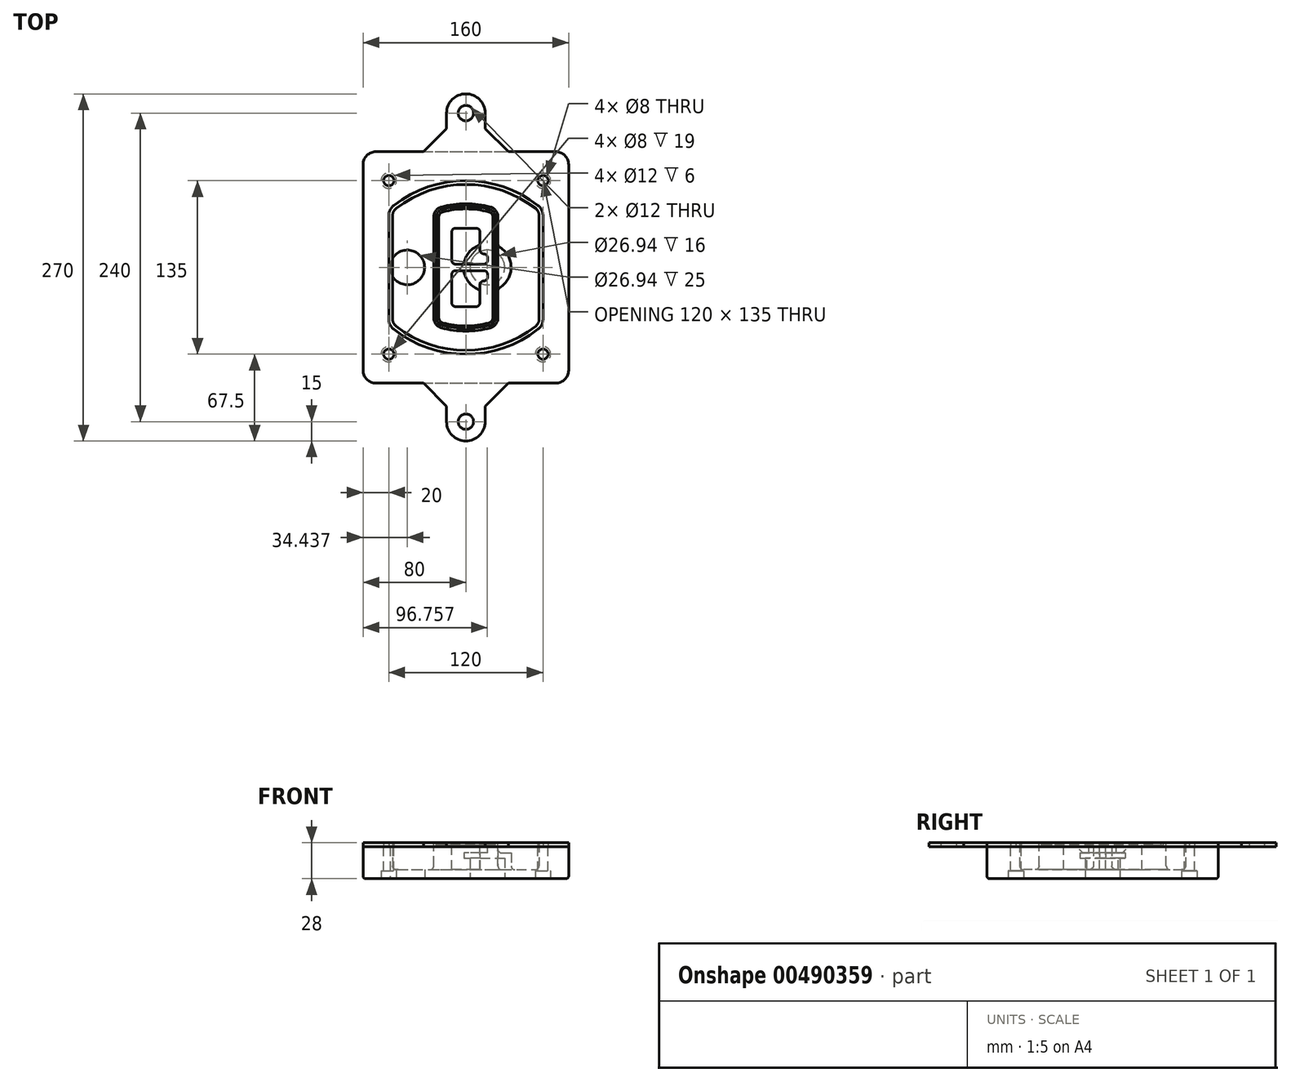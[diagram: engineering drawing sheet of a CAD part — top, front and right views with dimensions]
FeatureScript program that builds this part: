
annotation { "Feature Type Name" : "Feature", "Feature Type Description" : "" }
export const myFeature = defineFeature(function(context is Context, id is Id, definition is map)
    precondition{}
    {
        {
            var Q0;
            Q0=qCreatedBy(makeId("Top.planeOp"),FACE);
            var sketch = newSketch(context, id + "F0", { "sketchPlane" : qUnion([Q0])});
            skPoint(sketch, "E0.rect.middle", {"position": v(0, 0) * mm});
            skLineSegment(sketch, "E1.bottom", {"start": v(-70, -90) * mm, "end": v(70, -90) * mm});
            skLineSegment(sketch, "E1.top", {"start": v(-70, 90) * mm, "end": v(70, 90) * mm});
            skLineSegment(sketch, "E1.left", {"start": v(-80, -80) * mm, "end": v(-80, 80) * mm});
            skLineSegment(sketch, "E1.right", {"start": v(80, -80) * mm, "end": v(80, 80) * mm});
            skLineSegment(sketch, "E2", {"start": v(-80, 90) * mm, "end": v(80, -90) * mm, "construction": true});
            skLineSegment(sketch, "E3", {"start": v(80, 90) * mm, "end": v(-80, -90) * mm, "construction": true});
            skCircle(sketch, "E4", {"center": v(-60, 67.5) * mm, "radius": 4 * mm});
            skCircle(sketch, "E5", {"center": v(60, 67.5) * mm, "radius": 4 * mm});
            skCircle(sketch, "E6", {"center": v(60, -67.5) * mm, "radius": 4 * mm});
            skCircle(sketch, "E7", {"center": v(-60, -67.5) * mm, "radius": 4 * mm});
            skLineSegment(sketch, "E8", {"start": v(-60, 67.5) * mm, "end": v(60, 67.5) * mm, "construction": true});
            skLineSegment(sketch, "E9", {"start": v(60, 67.5) * mm, "end": v(60, -67.5) * mm, "construction": true});
            skLineSegment(sketch, "E10", {"start": v(60, -67.5) * mm, "end": v(-60, -67.5) * mm, "construction": true});
            skLineSegment(sketch, "E11", {"start": v(-60, -67.5) * mm, "end": v(-60, 67.5) * mm, "construction": true});
            skLineSegment(sketch, "E12", {"start": v(-60, 40.3) * mm, "end": v(-60, -40.3) * mm});
            skLineSegment(sketch, "E13", {"start": v(60, 40.3) * mm, "end": v(60, -40.3) * mm});
            skArc(sketch, "E14", {"start": v(56.15, 48.18) * mm, "mid": v(0, 67.5) * mm, "end": v(-56.15, 48.18) * mm});
            skArc(sketch, "E15", {"start": v(-56.15, -48.18) * mm, "mid": v(0, -67.5) * mm, "end": v(56.15, -48.18) * mm});
            skLineSegment(sketch, "E16", {"start": v(-60, 0) * mm, "end": v(60, 0) * mm, "construction": true});
            skPoint(sketch, "E17.visualSharp", {"position": v(-60, -45) * mm});
            skArc(sketch, "E17.filletArc", {"start": v(-60, -40.3) * mm, "mid": v(-58.99, -44.68) * mm, "end": v(-56.15, -48.18) * mm});
            skPoint(sketch, "E18.visualSharp", {"position": v(-60, 45) * mm});
            skArc(sketch, "E18.filletArc", {"start": v(-56.15, 48.18) * mm, "mid": v(-58.99, 44.68) * mm, "end": v(-60, 40.3) * mm});
            skPoint(sketch, "E19.visualSharp", {"position": v(60, 45) * mm});
            skArc(sketch, "E19.filletArc", {"start": v(60, 40.3) * mm, "mid": v(58.99, 44.68) * mm, "end": v(56.15, 48.18) * mm});
            skPoint(sketch, "E20.visualSharp", {"position": v(60, -45) * mm});
            skArc(sketch, "E20.filletArc", {"start": v(56.15, -48.18) * mm, "mid": v(58.99, -44.68) * mm, "end": v(60, -40.3) * mm});
            skPoint(sketch, "E21.visualSharp", {"position": v(-80, 90) * mm});
            skArc(sketch, "E21.filletArc", {"start": v(-70, 90) * mm, "mid": v(-77.07, 87.07) * mm, "end": v(-80, 80) * mm});
            skPoint(sketch, "E22.visualSharp", {"position": v(80, 90) * mm});
            skArc(sketch, "E22.filletArc", {"start": v(80, 80) * mm, "mid": v(77.07, 87.07) * mm, "end": v(70, 90) * mm});
            skPoint(sketch, "E23.visualSharp", {"position": v(80, -90) * mm});
            skArc(sketch, "E23.filletArc", {"start": v(70, -90) * mm, "mid": v(77.07, -87.07) * mm, "end": v(80, -80) * mm});
            skPoint(sketch, "E24.visualSharp", {"position": v(-80, -90) * mm});
            skArc(sketch, "E24.filletArc", {"start": v(-80, -80) * mm, "mid": v(-77.07, -87.07) * mm, "end": v(-70, -90) * mm});
            skArc(sketch, "E25.0", {"start": v(57, 40.3) * mm, "mid": v(56.3, 43.36) * mm, "end": v(54.3, 45.81) * mm});
            skLineSegment(sketch, "E25.1", {"start": v(57, 40.3) * mm, "end": v(57, -40.3) * mm});
            skArc(sketch, "E25.2", {"start": v(54.3, -45.81) * mm, "mid": v(56.3, -43.36) * mm, "end": v(57, -40.3) * mm});
            skArc(sketch, "E25.3", {"start": v(-54.3, -45.81) * mm, "mid": v(0, -64.5) * mm, "end": v(54.3, -45.81) * mm});
            skArc(sketch, "E25.4", {"start": v(-57, -40.3) * mm, "mid": v(-56.3, -43.36) * mm, "end": v(-54.3, -45.81) * mm});
            skArc(sketch, "E25.5", {"start": v(54.3, 45.81) * mm, "mid": v(0, 64.5) * mm, "end": v(-54.3, 45.81) * mm});
            skLineSegment(sketch, "E25.6", {"start": v(-57, 40.3) * mm, "end": v(-57, -40.3) * mm});
            skArc(sketch, "E25.7", {"start": v(-54.3, 45.81) * mm, "mid": v(-56.3, 43.36) * mm, "end": v(-57, 40.3) * mm});
            skArc(sketch, "E26.0", {"start": v(-58.62, 51.33) * mm, "mid": v(-62.58, 46.43) * mm, "end": v(-64, 40.3) * mm});
            skArc(sketch, "E26.1", {"start": v(58.62, 51.33) * mm, "mid": v(0, 71.5) * mm, "end": v(-58.62, 51.33) * mm});
            skArc(sketch, "E26.2", {"start": v(64, 40.3) * mm, "mid": v(62.58, 46.43) * mm, "end": v(58.62, 51.33) * mm});
            skLineSegment(sketch, "E26.3", {"start": v(64, 40.3) * mm, "end": v(64, -40.3) * mm});
            skArc(sketch, "E26.4", {"start": v(58.62, -51.33) * mm, "mid": v(62.58, -46.43) * mm, "end": v(64, -40.3) * mm});
            skLineSegment(sketch, "E26.5", {"start": v(-64, 40.3) * mm, "end": v(-64, -40.3) * mm});
            skArc(sketch, "E26.6", {"start": v(-58.62, -51.33) * mm, "mid": v(0, -71.5) * mm, "end": v(58.62, -51.33) * mm});
            skArc(sketch, "E26.7", {"start": v(-64, -40.3) * mm, "mid": v(-62.58, -46.43) * mm, "end": v(-58.62, -51.33) * mm});
            skSolve(sketch);
        }
        {
            var Q0;
            Q0=makeQuery(id+"F0.imprint","IMPRINT",FACE,{"disambiguationData":[TD([[makeQuery(id+"F0.imprint","IMPRINT",EDGE,{"derivedFrom":sQuery(id+"F0.wireOp",EDGE,"E1.bottom")}),1.0]])]});
            var Q1;
            Q1=makeQuery(id+"F0.imprint","IMPRINT",FACE,{"disambiguationData":[TD([[makeQuery(id+"F0.imprint","IMPRINT",EDGE,{"derivedFrom":sQuery(id+"F0.wireOp",EDGE,"E12")}),1.0]])]});
            var Q2;
            Q2=makeQuery(id+"F0.imprint","IMPRINT",FACE,{"disambiguationData":[TD([[makeQuery(id+"F0.imprint","IMPRINT",EDGE,{"derivedFrom":sQuery(id+"F0.wireOp",EDGE,"E25.0")}),1.0]])]});
            var Q3;
            Q3=makeQuery(id+"F0.imprint","IMPRINT",FACE,{"disambiguationData":[TD([[makeQuery(id+"F0.imprint","IMPRINT",EDGE,{"derivedFrom":sQuery(id+"F0.wireOp",EDGE,"E12")}),-1.0]])]});
            extrude(context, id + "F1", {"entities" : qUnion([Q0, Q1, Q2, Q3]), "oppositeDirection" : true, "depth" : 25 * mm});
        }
        {
            var Q0;
            Q0=makeQuery(id+"F0.imprint","IMPRINT",FACE,{"disambiguationData":[TD([[makeQuery(id+"F0.imprint","IMPRINT",EDGE,{"derivedFrom":sQuery(id+"F0.wireOp",EDGE,"E12")}),1.0]])]});
            extrude(context, id + "F2", {"entities" : qUnion([Q0]), "operationType" : NewBodyOperationType.ADD, "depth" : 3 * mm});
        }
        {
            var Q0;
            Q0=makeQuery(id+"F0.imprint","IMPRINT",FACE,{"disambiguationData":[TD([[makeQuery(id+"F0.imprint","IMPRINT",EDGE,{"derivedFrom":sQuery(id+"F0.wireOp",EDGE,"E25.0")}),1.0]])]});
            extrude(context, id + "F3", {"entities" : qUnion([Q0]), "operationType" : NewBodyOperationType.REMOVE, "oppositeDirection" : true, "depth" : 18 * mm});
        }
        {
            var Q0;
            Q0=makeQuery(id+"F2.opExtrude","CAP_FACE",FACE,{"disambiguationData":[OSD([sQuery(id+"F0.wireOp",EDGE,"E12"),sQuery(id+"F0.wireOp",EDGE,"E13"),sQuery(id+"F0.wireOp",EDGE,"E14"),sQuery(id+"F0.wireOp",EDGE,"E15"),sQuery(id+"F0.wireOp",EDGE,"E17.filletArc"),sQuery(id+"F0.wireOp",EDGE,"E18.filletArc"),sQuery(id+"F0.wireOp",EDGE,"E19.filletArc"),sQuery(id+"F0.wireOp",EDGE,"E20.filletArc"),sQuery(id+"F0.wireOp",EDGE,"E25.0"),sQuery(id+"F0.wireOp",EDGE,"E25.1"),sQuery(id+"F0.wireOp",EDGE,"E25.2"),sQuery(id+"F0.wireOp",EDGE,"E25.3"),sQuery(id+"F0.wireOp",EDGE,"E25.4"),sQuery(id+"F0.wireOp",EDGE,"E25.5"),sQuery(id+"F0.wireOp",EDGE,"E25.6"),sQuery(id+"F0.wireOp",EDGE,"E25.7")])],"isStart":false});
            var sketch = newSketch(context, id + "F4", { "sketchPlane" : qUnion([Q0])});
            skArc(sketch, "E27.0", {"start": v(-19.08, -46.97) * mm, "mid": v(0, -49.5) * mm, "end": v(19.08, -46.97) * mm});
            skArc(sketch, "E28.0", {"start": v(19.08, 46.97) * mm, "mid": v(0, 49.5) * mm, "end": v(-19.08, 46.97) * mm});
            skLineSegment(sketch, "E29", {"start": v(-25, 39.25) * mm, "end": v(-25, -39.25) * mm});
            skLineSegment(sketch, "E30", {"start": v(25, 39.25) * mm, "end": v(25, -39.25) * mm});
            skLineSegment(sketch, "E31", {"start": v(-25, 45.1) * mm, "end": v(25, 45.1) * mm, "construction": true});
            skLineSegment(sketch, "E32", {"start": v(-25, -45.1) * mm, "end": v(25, -45.1) * mm, "construction": true});
            skPoint(sketch, "E33.visualSharp", {"position": v(-25, 45.1) * mm});
            skArc(sketch, "E33.filletArc", {"start": v(-19.08, 46.97) * mm, "mid": v(-23.35, 44.11) * mm, "end": v(-25, 39.25) * mm});
            skPoint(sketch, "E34.visualSharp", {"position": v(25, 45.1) * mm});
            skArc(sketch, "E34.filletArc", {"start": v(25, 39.25) * mm, "mid": v(23.35, 44.11) * mm, "end": v(19.08, 46.97) * mm});
            skPoint(sketch, "E35.visualSharp", {"position": v(25, -45.1) * mm});
            skArc(sketch, "E35.filletArc", {"start": v(19.08, -46.97) * mm, "mid": v(23.35, -44.11) * mm, "end": v(25, -39.25) * mm});
            skPoint(sketch, "E36.visualSharp", {"position": v(-25, -45.1) * mm});
            skArc(sketch, "E36.filletArc", {"start": v(-25, -39.25) * mm, "mid": v(-23.35, -44.11) * mm, "end": v(-19.08, -46.97) * mm});
            skArc(sketch, "E37.0", {"start": v(54.3, 45.81) * mm, "mid": v(0, 64.5) * mm, "end": v(-54.3, 45.81) * mm});
            skArc(sketch, "E37.1", {"start": v(-54.3, 45.81) * mm, "mid": v(-56.3, 43.36) * mm, "end": v(-57, 40.3) * mm});
            skLineSegment(sketch, "E37.2", {"start": v(-57, 40.3) * mm, "end": v(-57, -40.3) * mm});
            skArc(sketch, "E37.3", {"start": v(-57, -40.3) * mm, "mid": v(-56.3, -43.36) * mm, "end": v(-54.3, -45.81) * mm});
            skArc(sketch, "E37.4", {"start": v(-54.3, -45.81) * mm, "mid": v(0, -64.5) * mm, "end": v(54.3, -45.81) * mm});
            skArc(sketch, "E37.5", {"start": v(54.3, -45.81) * mm, "mid": v(56.3, -43.36) * mm, "end": v(57, -40.3) * mm});
            skLineSegment(sketch, "E37.6", {"start": v(57, 40.3) * mm, "end": v(57, -40.3) * mm});
            skArc(sketch, "E37.7", {"start": v(57, 40.3) * mm, "mid": v(56.3, 43.36) * mm, "end": v(54.3, 45.81) * mm});
            skLineSegment(sketch, "E38.0", {"start": v(23, 39.25) * mm, "end": v(23, -39.25) * mm});
            skArc(sketch, "E38.1", {"start": v(18.56, -45.04) * mm, "mid": v(21.76, -42.9) * mm, "end": v(23, -39.25) * mm});
            skArc(sketch, "E38.2", {"start": v(-18.56, -45.04) * mm, "mid": v(0, -47.5) * mm, "end": v(18.56, -45.04) * mm});
            skArc(sketch, "E38.3", {"start": v(-23, -39.25) * mm, "mid": v(-21.76, -42.9) * mm, "end": v(-18.56, -45.04) * mm});
            skLineSegment(sketch, "E38.4", {"start": v(-23, 39.25) * mm, "end": v(-23, -39.25) * mm});
            skArc(sketch, "E38.5", {"start": v(23, 39.25) * mm, "mid": v(21.76, 42.9) * mm, "end": v(18.56, 45.04) * mm});
            skArc(sketch, "E38.6", {"start": v(-18.56, 45.04) * mm, "mid": v(-21.76, 42.9) * mm, "end": v(-23, 39.25) * mm});
            skArc(sketch, "E38.7", {"start": v(18.56, 45.04) * mm, "mid": v(0, 47.5) * mm, "end": v(-18.56, 45.04) * mm});
            skArc(sketch, "E39.0", {"start": v(21, 39.25) * mm, "mid": v(20.18, 41.68) * mm, "end": v(18.04, 43.1) * mm});
            skLineSegment(sketch, "E39.1", {"start": v(21, 39.25) * mm, "end": v(21, -39.25) * mm});
            skArc(sketch, "E39.2", {"start": v(18.04, -43.1) * mm, "mid": v(20.18, -41.68) * mm, "end": v(21, -39.25) * mm});
            skArc(sketch, "E39.3", {"start": v(-18.04, -43.1) * mm, "mid": v(0, -45.5) * mm, "end": v(18.04, -43.1) * mm});
            skArc(sketch, "E39.4", {"start": v(-21, -39.25) * mm, "mid": v(-20.18, -41.68) * mm, "end": v(-18.04, -43.1) * mm});
            skArc(sketch, "E39.5", {"start": v(18.04, 43.1) * mm, "mid": v(0, 45.5) * mm, "end": v(-18.04, 43.1) * mm});
            skLineSegment(sketch, "E39.6", {"start": v(-21, 39.25) * mm, "end": v(-21, -39.25) * mm});
            skArc(sketch, "E39.7", {"start": v(-18.04, 43.1) * mm, "mid": v(-20.18, 41.68) * mm, "end": v(-21, 39.25) * mm});
            skLineSegment(sketch, "E40", {"start": v(-25, 0) * mm, "end": v(25, 0) * mm, "construction": true});
            skLineSegment(sketch, "E41", {"start": v(-11, 5.5) * mm, "end": v(-11, 27.5) * mm});
            skLineSegment(sketch, "E42", {"start": v(-8, 30.5) * mm, "end": v(8, 30.5) * mm});
            skLineSegment(sketch, "E43", {"start": v(11, 27.5) * mm, "end": v(11, 13.5) * mm});
            skLineSegment(sketch, "E44", {"start": v(14, 10.5) * mm, "end": v(14, 10.5) * mm});
            skLineSegment(sketch, "E45", {"start": v(17, 7.5) * mm, "end": v(17, 5.5) * mm});
            skLineSegment(sketch, "E46", {"start": v(14, 2.5) * mm, "end": v(-8, 2.5) * mm});
            skPoint(sketch, "E47.visualSharp", {"position": v(-11, 30.5) * mm});
            skArc(sketch, "E47.filletArc", {"start": v(-8, 30.5) * mm, "mid": v(-10.12, 29.62) * mm, "end": v(-11, 27.5) * mm});
            skPoint(sketch, "E48.visualSharp", {"position": v(11, 30.5) * mm});
            skArc(sketch, "E48.filletArc", {"start": v(11, 27.5) * mm, "mid": v(10.12, 29.62) * mm, "end": v(8, 30.5) * mm});
            skPoint(sketch, "E49.visualSharp", {"position": v(11, 10.5) * mm});
            skArc(sketch, "E49.filletArc", {"start": v(11, 13.5) * mm, "mid": v(11.88, 11.38) * mm, "end": v(14, 10.5) * mm});
            skPoint(sketch, "E50.visualSharp", {"position": v(17, 10.5) * mm});
            skArc(sketch, "E50.filletArc", {"start": v(17, 7.5) * mm, "mid": v(16.12, 9.62) * mm, "end": v(14, 10.5) * mm});
            skPoint(sketch, "E51.visualSharp", {"position": v(17, 2.5) * mm});
            skArc(sketch, "E51.filletArc", {"start": v(14, 2.5) * mm, "mid": v(16.12, 3.38) * mm, "end": v(17, 5.5) * mm});
            skPoint(sketch, "E52.visualSharp", {"position": v(-11, 2.5) * mm});
            skArc(sketch, "E52.filletArc", {"start": v(-11, 5.5) * mm, "mid": v(-10.12, 3.38) * mm, "end": v(-8, 2.5) * mm});
            skLineSegment(sketch, "E53.0.MirrorCS", {"start": v(14, -2.5) * mm, "end": v(-8, -2.5) * mm});
            skArc(sketch, "E54.0.MirrorCS", {"start": v(-11, -5.5) * mm, "mid": v(-10.12, -3.38) * mm, "end": v(-8, -2.5) * mm});
            skLineSegment(sketch, "E55.0.MirrorCS", {"start": v(-11, -5.5) * mm, "end": v(-11, -27.5) * mm});
            skArc(sketch, "E56.0.MirrorCS", {"start": v(-8, -30.5) * mm, "mid": v(-10.12, -29.62) * mm, "end": v(-11, -27.5) * mm});
            skLineSegment(sketch, "E57.0.MirrorCS", {"start": v(-8, -30.5) * mm, "end": v(8, -30.5) * mm});
            skArc(sketch, "E58.0.MirrorCS", {"start": v(11, -27.5) * mm, "mid": v(10.12, -29.62) * mm, "end": v(8, -30.5) * mm});
            skLineSegment(sketch, "E59.0.MirrorCS", {"start": v(11, -27.5) * mm, "end": v(11, -13.5) * mm});
            skArc(sketch, "E60.0.MirrorCS", {"start": v(11, -13.5) * mm, "mid": v(11.88, -11.38) * mm, "end": v(14, -10.5) * mm});
            skArc(sketch, "E61.0.MirrorCS", {"start": v(17, -7.5) * mm, "mid": v(16.12, -9.62) * mm, "end": v(14, -10.5) * mm});
            skLineSegment(sketch, "E62.0.MirrorCS", {"start": v(17, -7.5) * mm, "end": v(17, -5.5) * mm});
            skArc(sketch, "E63.0.MirrorCS", {"start": v(14, -2.5) * mm, "mid": v(16.12, -3.38) * mm, "end": v(17, -5.5) * mm});
            skSolve(sketch);
        }
        {
            var Q0;
            Q0=makeQuery(id+"F4.imprint","IMPRINT",FACE,{"disambiguationData":[TD([[makeQuery(id+"F4.imprint","IMPRINT",EDGE,{"derivedFrom":sQuery(id+"F4.wireOp",EDGE,"E27.0")}),1.0]])]});
            var Q1;
            Q1=makeQuery(id+"F4.imprint","IMPRINT",FACE,{"disambiguationData":[TD([[makeQuery(id+"F4.imprint","IMPRINT",EDGE,{"derivedFrom":sQuery(id+"F4.wireOp",EDGE,"E38.0")}),-1.0]])]});
            var Q2;
            Q2=makeQuery(id+"F4.imprint","IMPRINT",FACE,{"disambiguationData":[TD([[makeQuery(id+"F4.imprint","IMPRINT",EDGE,{"derivedFrom":sQuery(id+"F4.wireOp",EDGE,"E39.0")}),1.0]])]});
            extrude(context, id + "F5", {"entities" : qUnion([Q0, Q1, Q2]), "operationType" : NewBodyOperationType.ADD, "endBound" : BoundingType.UP_TO_NEXT, "oppositeDirection" : true, "depth" : 25 * mm});
        }
        {
            var Q0;
            Q0=makeQuery(id+"F4.imprint","IMPRINT",FACE,{"disambiguationData":[TD([[makeQuery(id+"F4.imprint","IMPRINT",EDGE,{"derivedFrom":sQuery(id+"F4.wireOp",EDGE,"E38.0")}),-1.0]])]});
            extrude(context, id + "F6", {"entities" : qUnion([Q0]), "operationType" : NewBodyOperationType.REMOVE, "oppositeDirection" : true, "depth" : 2 * mm});
        }
        {
            var Q0;
            Q0=makeQuery(id+"F1.opExtrude","CAP_FACE",FACE,{"disambiguationData":[OSD([sQuery(id+"F0.wireOp",EDGE,"E1.bottom"),sQuery(id+"F0.wireOp",EDGE,"E1.top"),sQuery(id+"F0.wireOp",EDGE,"E1.left"),sQuery(id+"F0.wireOp",EDGE,"E1.right"),sQuery(id+"F0.wireOp",EDGE,"E4"),sQuery(id+"F0.wireOp",EDGE,"E5"),sQuery(id+"F0.wireOp",EDGE,"E6"),sQuery(id+"F0.wireOp",EDGE,"E7"),sQuery(id+"F0.wireOp",EDGE,"E21.filletArc"),sQuery(id+"F0.wireOp",EDGE,"E22.filletArc"),sQuery(id+"F0.wireOp",EDGE,"E23.filletArc"),sQuery(id+"F0.wireOp",EDGE,"E24.filletArc")])],"isStart":false});
            var sketch = newSketch(context, id + "F7", { "sketchPlane" : qUnion([Q0])});
            skCircle(sketch, "E64", {"center": v(16.76, 0) * mm, "radius": 13.47 * mm});
            skCircle(sketch, "E65", {"center": v(-45.56, 0) * mm, "radius": 13.47 * mm});
            skLineSegment(sketch, "E66", {"start": v(80, 0) * mm, "end": v(-80, 0) * mm});
            skCircle(sketch, "E67", {"center": v(16.76, 0) * mm, "radius": 18.47 * mm});
            skCircle(sketch, "E68", {"center": v(60, -67.5) * mm, "radius": 6 * mm});
            skCircle(sketch, "E69", {"center": v(-60, -67.5) * mm, "radius": 6 * mm});
            skCircle(sketch, "E70", {"center": v(-60, 67.5) * mm, "radius": 6 * mm});
            skCircle(sketch, "E71", {"center": v(60, 67.5) * mm, "radius": 6 * mm});
            skSolve(sketch);
        }
        {
            var Q0;
            {var subQ1=sQuery(id+"F7.wireOp",EDGE,"E66");var subQ4=sQuery(id+"F7.wireOp",EDGE,"E64");var subQ6=makeQuery(id+"F7.imprint","INTERSECT",VERTEX,{"disambiguationData":[OD(0.0)],"derivedFrom":[subQ4,subQ1]});Q0=makeQuery(id+"F7.imprint","IMPRINT",FACE,{"disambiguationData":[TD([[makeQuery(id+"F7.imprint","IMPRINT",EDGE,{"disambiguationData":[TD([[subQ6,-1.0]])],"derivedFrom":subQ4}),-1.0]])]});}
            var Q1;
            {var subQ0=sQuery(id+"F7.wireOp",EDGE,"E66");var subQ1=sQuery(id+"F7.wireOp",EDGE,"E64");var subQ3=makeQuery(id+"F7.imprint","INTERSECT",VERTEX,{"disambiguationData":[OD(0.0)],"derivedFrom":[subQ1,subQ0]});Q1=makeQuery(id+"F7.imprint","IMPRINT",FACE,{"disambiguationData":[TD([[makeQuery(id+"F7.imprint","IMPRINT",EDGE,{"disambiguationData":[TD([[subQ3,-1.0]])],"derivedFrom":subQ1}),1.0]])]});}
            var Q2;
            {var subQ0=sQuery(id+"F7.wireOp",EDGE,"E66");var subQ1=sQuery(id+"F7.wireOp",EDGE,"E64");var subQ3=makeQuery(id+"F7.imprint","INTERSECT",VERTEX,{"disambiguationData":[OD(0.0)],"derivedFrom":[subQ1,subQ0]});Q2=makeQuery(id+"F7.imprint","IMPRINT",FACE,{"disambiguationData":[TD([[makeQuery(id+"F7.imprint","IMPRINT",EDGE,{"disambiguationData":[TD([[subQ3,1.0]])],"derivedFrom":subQ1}),1.0]])]});}
            var Q3;
            {var subQ1=sQuery(id+"F7.wireOp",EDGE,"E66");var subQ4=sQuery(id+"F7.wireOp",EDGE,"E64");var subQ6=makeQuery(id+"F7.imprint","INTERSECT",VERTEX,{"disambiguationData":[OD(0.0)],"derivedFrom":[subQ4,subQ1]});Q3=makeQuery(id+"F7.imprint","IMPRINT",FACE,{"disambiguationData":[TD([[makeQuery(id+"F7.imprint","IMPRINT",EDGE,{"disambiguationData":[TD([[subQ6,1.0]])],"derivedFrom":subQ4}),-1.0]])]});}
            extrude(context, id + "F8", {"entities" : qUnion([Q0, Q1, Q2, Q3]), "operationType" : NewBodyOperationType.ADD, "oppositeDirection" : true, "depth" : 20 * mm});
        }
        {
            var Q0;
            {var subQ0=sQuery(id+"F7.wireOp",EDGE,"E66");var subQ1=sQuery(id+"F7.wireOp",EDGE,"E64");var subQ3=makeQuery(id+"F7.imprint","INTERSECT",VERTEX,{"disambiguationData":[OD(0.0)],"derivedFrom":[subQ1,subQ0]});Q0=makeQuery(id+"F7.imprint","IMPRINT",FACE,{"disambiguationData":[TD([[makeQuery(id+"F7.imprint","IMPRINT",EDGE,{"disambiguationData":[TD([[subQ3,-1.0]])],"derivedFrom":subQ1}),1.0]])]});}
            var Q1;
            {var subQ0=sQuery(id+"F7.wireOp",EDGE,"E66");var subQ1=sQuery(id+"F7.wireOp",EDGE,"E64");var subQ3=makeQuery(id+"F7.imprint","INTERSECT",VERTEX,{"disambiguationData":[OD(0.0)],"derivedFrom":[subQ1,subQ0]});Q1=makeQuery(id+"F7.imprint","IMPRINT",FACE,{"disambiguationData":[TD([[makeQuery(id+"F7.imprint","IMPRINT",EDGE,{"disambiguationData":[TD([[subQ3,1.0]])],"derivedFrom":subQ1}),1.0]])]});}
            extrude(context, id + "F9", {"entities" : qUnion([Q0, Q1]), "operationType" : NewBodyOperationType.REMOVE, "oppositeDirection" : true, "depth" : 16 * mm});
        }
        {
            var Q0;
            {var subQ0=sQuery(id+"F7.wireOp",EDGE,"E66");var subQ1=sQuery(id+"F7.wireOp",EDGE,"E65");var subQ3=makeQuery(id+"F7.imprint","INTERSECT",VERTEX,{"disambiguationData":[OD(0.0)],"derivedFrom":[subQ1,subQ0]});Q0=makeQuery(id+"F7.imprint","IMPRINT",FACE,{"disambiguationData":[TD([[makeQuery(id+"F7.imprint","IMPRINT",EDGE,{"disambiguationData":[TD([[subQ3,-1.0]])],"derivedFrom":subQ1}),1.0]])]});}
            var Q1;
            {var subQ0=sQuery(id+"F7.wireOp",EDGE,"E66");var subQ1=sQuery(id+"F7.wireOp",EDGE,"E65");var subQ3=makeQuery(id+"F7.imprint","INTERSECT",VERTEX,{"disambiguationData":[OD(0.0)],"derivedFrom":[subQ1,subQ0]});Q1=makeQuery(id+"F7.imprint","IMPRINT",FACE,{"disambiguationData":[TD([[makeQuery(id+"F7.imprint","IMPRINT",EDGE,{"disambiguationData":[TD([[subQ3,1.0]])],"derivedFrom":subQ1}),1.0]])]});}
            extrude(context, id + "F10", {"entities" : qUnion([Q0, Q1]), "operationType" : NewBodyOperationType.REMOVE, "oppositeDirection" : true, "depth" : 25 * mm});
        }
        {
            var Q0;
            Q0=makeQuery(id+"F7.imprint","IMPRINT",FACE,{"disambiguationData":[TD([[makeQuery(id+"F7.imprint","IMPRINT",EDGE,{"derivedFrom":sQuery(id+"F7.wireOp",EDGE,"E68")}),1.0]])]});
            var Q1;
            Q1=makeQuery(id+"F7.imprint","IMPRINT",FACE,{"disambiguationData":[TD([[makeQuery(id+"F7.imprint","IMPRINT",EDGE,{"derivedFrom":makeQuery(id+"F1.opExtrude","CAP_EDGE",EDGE,{"disambiguationData":[OSD([sQuery(id+"F0.wireOp",EDGE,"E5")])],"isStart":false})}),-1.0]])]});
            var Q2;
            Q2=makeQuery(id+"F7.imprint","IMPRINT",FACE,{"disambiguationData":[TD([[makeQuery(id+"F7.imprint","IMPRINT",EDGE,{"derivedFrom":sQuery(id+"F7.wireOp",EDGE,"E69")}),1.0]])]});
            var Q3;
            Q3=makeQuery(id+"F7.imprint","IMPRINT",FACE,{"disambiguationData":[TD([[makeQuery(id+"F7.imprint","IMPRINT",EDGE,{"derivedFrom":makeQuery(id+"F1.opExtrude","CAP_EDGE",EDGE,{"disambiguationData":[OSD([sQuery(id+"F0.wireOp",EDGE,"E4")])],"isStart":false})}),-1.0]])]});
            var Q4;
            Q4=makeQuery(id+"F7.imprint","IMPRINT",FACE,{"disambiguationData":[TD([[makeQuery(id+"F7.imprint","IMPRINT",EDGE,{"derivedFrom":sQuery(id+"F7.wireOp",EDGE,"E70")}),1.0]])]});
            var Q5;
            Q5=makeQuery(id+"F7.imprint","IMPRINT",FACE,{"disambiguationData":[TD([[makeQuery(id+"F7.imprint","IMPRINT",EDGE,{"derivedFrom":makeQuery(id+"F1.opExtrude","CAP_EDGE",EDGE,{"disambiguationData":[OSD([sQuery(id+"F0.wireOp",EDGE,"E7")])],"isStart":false})}),-1.0]])]});
            var Q6;
            Q6=makeQuery(id+"F7.imprint","IMPRINT",FACE,{"disambiguationData":[TD([[makeQuery(id+"F7.imprint","IMPRINT",EDGE,{"derivedFrom":sQuery(id+"F7.wireOp",EDGE,"E71")}),1.0]])]});
            var Q7;
            Q7=makeQuery(id+"F7.imprint","IMPRINT",FACE,{"disambiguationData":[TD([[makeQuery(id+"F7.imprint","IMPRINT",EDGE,{"derivedFrom":makeQuery(id+"F1.opExtrude","CAP_EDGE",EDGE,{"disambiguationData":[OSD([sQuery(id+"F0.wireOp",EDGE,"E6")])],"isStart":false})}),-1.0]])]});
            extrude(context, id + "F11", {"entities" : qUnion([Q0, Q1, Q2, Q3, Q4, Q5, Q6, Q7]), "operationType" : NewBodyOperationType.REMOVE, "oppositeDirection" : true, "depth" : 6 * mm});
        }
        {
            var Q0;
            Q0=makeQuery(id+"F9.boolean.opBoolean","COPY",FACE,{"derivedFrom":makeQuery(id+"F9.opExtrude","CAP_FACE",FACE,{"disambiguationData":[OSD([sQuery(id+"F7.wireOp",EDGE,"E64")])],"isStart":false})});
            var sketch = newSketch(context, id + "F12", { "sketchPlane" : qUnion([Q0])});
            skArc(sketch, "E72.0", {"start": v(11, 17.55) * mm, "mid": v(2.57, 11.82) * mm, "end": v(-1.54, 2.5) * mm});
            skArc(sketch, "E72.1", {"start": v(-1.54, -2.5) * mm, "mid": v(2.57, -11.82) * mm, "end": v(11, -17.55) * mm});
            skLineSegment(sketch, "E73", {"start": v(-1.54, -2.5) * mm, "end": v(14, -2.5) * mm});
            skLineSegment(sketch, "E74.0", {"start": v(14, 2.5) * mm, "end": v(-1.54, 2.5) * mm});
            skArc(sketch, "E74.1", {"start": v(14, 2.5) * mm, "mid": v(16.12, 3.38) * mm, "end": v(17, 5.5) * mm});
            skLineSegment(sketch, "E74.2", {"start": v(17, 7.5) * mm, "end": v(17, 5.5) * mm});
            skArc(sketch, "E74.3", {"start": v(17, 7.5) * mm, "mid": v(16.12, 9.62) * mm, "end": v(14, 10.5) * mm});
            skArc(sketch, "E74.4", {"start": v(11, 13.5) * mm, "mid": v(11.88, 11.38) * mm, "end": v(14, 10.5) * mm});
            skLineSegment(sketch, "E74.5", {"start": v(11, 17.55) * mm, "end": v(11, 13.5) * mm});
            skLineSegment(sketch, "E74.7", {"start": v(14, -2.5) * mm, "end": v(-1.54, -2.5) * mm});
            skArc(sketch, "E74.8", {"start": v(14, -2.5) * mm, "mid": v(16.12, -3.38) * mm, "end": v(17, -5.5) * mm});
            skLineSegment(sketch, "E74.9", {"start": v(17, -7.5) * mm, "end": v(17, -5.5) * mm});
            skArc(sketch, "E74.10", {"start": v(17, -7.5) * mm, "mid": v(16.12, -9.62) * mm, "end": v(14, -10.5) * mm});
            skArc(sketch, "E74.11", {"start": v(11, -13.5) * mm, "mid": v(11.88, -11.38) * mm, "end": v(14, -10.5) * mm});
            skLineSegment(sketch, "E74.12", {"start": v(11, -17.55) * mm, "end": v(11, -13.5) * mm});
            skPoint(sketch, "E75.orphan", {"position": v(11, -27.5) * mm});
            skPoint(sketch, "E76.orphan", {"position": v(-8, -2.5) * mm});
            skPoint(sketch, "E77.orphan", {"position": v(-8, 2.5) * mm});
            skPoint(sketch, "E78.orphan", {"position": v(11, 27.5) * mm});
            skSolve(sketch);
        }
        {
            var Q0;
            {var subQ7=sQuery(id+"F12.wireOp",EDGE,"E72.0");var subQ14=sQuery(id+"F12.wireOp",EDGE,"E72.1");var subQ16=sQuery(id+"F12.wireOp",EDGE,"E74.1");var subQ18=sQuery(id+"F12.wireOp",EDGE,"E74.8");Q0=qUnion([makeQuery(id+"F12.imprint","IMPRINT",FACE,{"disambiguationData":[TD([[makeQuery(id+"F12.imprint","IMPRINT",EDGE,{"derivedFrom":subQ7}),1.0]])]}),makeQuery(id+"F12.imprint","IMPRINT",FACE,{"disambiguationData":[TD([[makeQuery(id+"F12.imprint","IMPRINT",EDGE,{"derivedFrom":subQ14}),1.0]])]}),makeQuery(id+"F12.imprint","IMPRINT",FACE,{"disambiguationData":[TD([[makeQuery(id+"F12.imprint","IMPRINT",EDGE,{"derivedFrom":subQ16}),1.0]])]}),makeQuery(id+"F12.imprint","IMPRINT",FACE,{"disambiguationData":[TD([[makeQuery(id+"F12.imprint","IMPRINT",EDGE,{"derivedFrom":subQ18}),-1.0]])]})]);}
            var Q1;
            Q1=makeQuery(id+"F5.boolean.opBoolean","SPLIT",FACE,{"disambiguationData":[TD([makeQuery(id+"F5.opExtrude","SWEPT_FACE",FACE,{"disambiguationData":[OSD([sQuery(id+"F4.wireOp",EDGE,"E41")])]})])],"derivedFrom":makeQuery(id+"F3.boolean.opBoolean","COPY",FACE,{"derivedFrom":makeQuery(id+"F3.opExtrude","CAP_FACE",FACE,{"disambiguationData":[OSD([sQuery(id+"F0.wireOp",EDGE,"E25.0"),sQuery(id+"F0.wireOp",EDGE,"E25.1"),sQuery(id+"F0.wireOp",EDGE,"E25.2"),sQuery(id+"F0.wireOp",EDGE,"E25.3"),sQuery(id+"F0.wireOp",EDGE,"E25.4"),sQuery(id+"F0.wireOp",EDGE,"E25.5"),sQuery(id+"F0.wireOp",EDGE,"E25.6"),sQuery(id+"F0.wireOp",EDGE,"E25.7")])],"isStart":false})})});
            extrude(context, id + "F13", {"entities" : qUnion([Q0]), "operationType" : NewBodyOperationType.REMOVE, "endBound" : BoundingType.UP_TO_SURFACE, "endBoundEntityFace" : qUnion([Q1]), "depth" : 25 * mm});
        }
        {
            var Q0;
            Q0=makeQuery(id+"F3.boolean.opBoolean","COPY",EDGE,{"derivedFrom":makeQuery(id+"F3.opExtrude","CAP_EDGE",EDGE,{"disambiguationData":[OSD([sQuery(id+"F0.wireOp",EDGE,"E25.6")])],"isStart":false})});
            var Q1;
            Q1=makeQuery(id+"F8.boolean.opBoolean","INTERSECT",EDGE,{"derivedFrom":[makeQuery(id+"F5.opExtrude","SWEPT_FACE",FACE,{"disambiguationData":[OSD([sQuery(id+"F4.wireOp",EDGE,"E30")])]}),makeQuery(id+"F8.opExtrude","CAP_FACE",FACE,{"disambiguationData":[OSD([sQuery(id+"F7.wireOp",EDGE,"E67")])],"isStart":false})]});
            var Q2;
            Q2=makeQuery(id+"F8.boolean.opBoolean","INTERSECT",EDGE,{"disambiguationData":[OD(1.0)],"derivedFrom":[makeQuery(id+"F5.opExtrude","SWEPT_FACE",FACE,{"disambiguationData":[OSD([sQuery(id+"F4.wireOp",EDGE,"E30")])]}),makeQuery(id+"F8.opExtrude","SWEPT_FACE",FACE,{"disambiguationData":[OSD([sQuery(id+"F7.wireOp",EDGE,"E67")])]})]});
            var Q3;
            {var subQ0=sQuery(id+"F4.wireOp",EDGE,"E30");Q3=makeQuery(id+"F8.boolean.opBoolean","SPLIT",EDGE,{"disambiguationData":[TD([makeQuery(id+"F5.opExtrude","SWEPT_FACE",FACE,{"disambiguationData":[OSD([sQuery(id+"F4.wireOp",EDGE,"E35.filletArc")])]})])],"derivedFrom":makeQuery(id+"F5.opExtrude","CAP_EDGE",EDGE,{"disambiguationData":[OSD([subQ0])],"isStart":false})});}
            var Q4;
            {var subQ0=sQuery(id+"F0.wireOp",EDGE,"E25.7");var subQ1=sQuery(id+"F0.wireOp",EDGE,"E25.1");var subQ2=sQuery(id+"F0.wireOp",EDGE,"E25.6");var subQ3=sQuery(id+"F0.wireOp",EDGE,"E25.5");var subQ4=sQuery(id+"F0.wireOp",EDGE,"E25.4");var subQ5=sQuery(id+"F0.wireOp",EDGE,"E25.0");var subQ6=sQuery(id+"F0.wireOp",EDGE,"E25.2");var subQ7=sQuery(id+"F0.wireOp",EDGE,"E25.3");Q4=makeQuery(id+"F8.boolean.opBoolean","INTERSECT",EDGE,{"derivedFrom":[makeQuery(id+"F5.boolean.opBoolean","SPLIT",FACE,{"disambiguationData":[TD([makeQuery(id+"F2.opExtrude","SWEPT_FACE",FACE,{"disambiguationData":[OSD([subQ5])]})])],"derivedFrom":makeQuery(id+"F3.boolean.opBoolean","COPY",FACE,{"derivedFrom":makeQuery(id+"F3.opExtrude","CAP_FACE",FACE,{"disambiguationData":[OSD([subQ5,subQ1,subQ6,subQ7,subQ4,subQ3,subQ2,subQ0])],"isStart":false})})}),makeQuery(id+"F8.opExtrude","SWEPT_FACE",FACE,{"disambiguationData":[OSD([sQuery(id+"F7.wireOp",EDGE,"E67")])]})]});}
            var Q5;
            Q5=makeQuery(id+"F8.boolean.opBoolean","INTERSECT",EDGE,{"disambiguationData":[OD(0.0)],"derivedFrom":[makeQuery(id+"F5.opExtrude","SWEPT_FACE",FACE,{"disambiguationData":[OSD([sQuery(id+"F4.wireOp",EDGE,"E30")])]}),makeQuery(id+"F8.opExtrude","SWEPT_FACE",FACE,{"disambiguationData":[OSD([sQuery(id+"F7.wireOp",EDGE,"E67")])]})]});
            fillet(context, id + "F14", {"entities" : qUnion([Q0, Q1, Q2, Q3, Q4, Q5]), "radius" : 3 * mm, "tangentPropagation" : true, "allowEdgeOverflow" : false});
        }
        {
            var Q0;
            Q0=makeQuery(id+"F1.opExtrude","CAP_EDGE",EDGE,{"disambiguationData":[OSD([sQuery(id+"F0.wireOp",EDGE,"E1.bottom")])],"isStart":false});
            fillet(context, id + "F15", {"entities" : qUnion([Q0]), "radius" : 2 * mm, "tangentPropagation" : true, "allowEdgeOverflow" : false});
        }
        {
            var Q0;
            Q0=qCreatedBy(makeId("Top.planeOp"),FACE);
            var sketch = newSketch(context, id + "F16", { "sketchPlane" : qUnion([Q0])});
            skLineSegment(sketch, "E79.0", {"start": v(-70, 90) * mm, "end": v(70, 90) * mm});
            skArc(sketch, "E79.1", {"start": v(-70, 90) * mm, "mid": v(-77.07, 87.07) * mm, "end": v(-80, 80) * mm});
            skArc(sketch, "E79.2", {"start": v(80, 80) * mm, "mid": v(77.07, 87.07) * mm, "end": v(70, 90) * mm});
            skLineSegment(sketch, "E79.3", {"start": v(80, -80) * mm, "end": v(80, 80) * mm});
            skLineSegment(sketch, "E79.4", {"start": v(-80, -80) * mm, "end": v(-80, 80) * mm});
            skArc(sketch, "E79.5", {"start": v(56.15, 48.18) * mm, "mid": v(0, 67.5) * mm, "end": v(-56.15, 48.18) * mm});
            skCircle(sketch, "E79.6", {"center": v(-60, 67.5) * mm, "radius": 4 * mm});
            skCircle(sketch, "E79.7", {"center": v(60, 67.5) * mm, "radius": 4 * mm});
            skArc(sketch, "E79.8", {"start": v(60, 40.3) * mm, "mid": v(58.99, 44.68) * mm, "end": v(56.15, 48.18) * mm});
            skLineSegment(sketch, "E79.9", {"start": v(60, 40.3) * mm, "end": v(60, -40.3) * mm});
            skArc(sketch, "E79.10", {"start": v(-56.15, 48.18) * mm, "mid": v(-58.99, 44.68) * mm, "end": v(-60, 40.3) * mm});
            skLineSegment(sketch, "E79.11", {"start": v(-60, 40.3) * mm, "end": v(-60, -40.3) * mm});
            skCircle(sketch, "E79.12", {"center": v(60, -67.5) * mm, "radius": 4 * mm});
            skArc(sketch, "E79.13", {"start": v(70, -90) * mm, "mid": v(77.07, -87.07) * mm, "end": v(80, -80) * mm});
            skLineSegment(sketch, "E79.14", {"start": v(-70, -90) * mm, "end": v(70, -90) * mm});
            skArc(sketch, "E79.15", {"start": v(-80, -80) * mm, "mid": v(-77.07, -87.07) * mm, "end": v(-70, -90) * mm});
            skArc(sketch, "E79.16", {"start": v(-56.15, -48.18) * mm, "mid": v(0, -67.5) * mm, "end": v(56.15, -48.18) * mm});
            skArc(sketch, "E79.17", {"start": v(-60, -40.3) * mm, "mid": v(-58.99, -44.68) * mm, "end": v(-56.15, -48.18) * mm});
            skArc(sketch, "E79.18", {"start": v(56.15, -48.18) * mm, "mid": v(58.99, -44.68) * mm, "end": v(60, -40.3) * mm});
            skCircle(sketch, "E79.19", {"center": v(-60, -67.5) * mm, "radius": 4 * mm});
            skLineSegment(sketch, "E80", {"start": v(0, 90) * mm, "end": v(0, 120) * mm, "construction": true});
            skPoint(sketch, "E80.endSnap0", {"position": v(0, 90) * mm});
            skCircle(sketch, "E81", {"center": v(0, 120) * mm, "radius": 6 * mm});
            skArc(sketch, "E82", {"start": v(-15, 120) * mm, "mid": v(0, 135) * mm, "end": v(15, 120) * mm});
            skLineSegment(sketch, "E83", {"start": v(-15, 120) * mm, "end": v(-15, 108) * mm});
            skLineSegment(sketch, "E84", {"start": v(-15, 108) * mm, "end": v(-33, 90) * mm});
            skLineSegment(sketch, "E85", {"start": v(15, 120) * mm, "end": v(15, 108) * mm});
            skLineSegment(sketch, "E86", {"start": v(15, 108) * mm, "end": v(33, 90) * mm});
            skLineSegment(sketch, "E87", {"start": v(-80, 0) * mm, "end": v(80, 0) * mm, "construction": true});
            skCircle(sketch, "E88.MirrorC", {"center": v(0, -120) * mm, "radius": 6 * mm});
            skLineSegment(sketch, "E89.MirrorCS", {"start": v(15, -120) * mm, "end": v(15, -108) * mm});
            skLineSegment(sketch, "E90.MirrorCS", {"start": v(-15, -120) * mm, "end": v(-15, -108) * mm});
            skLineSegment(sketch, "E91.MirrorCS", {"start": v(-15, -108) * mm, "end": v(-33, -90) * mm});
            skLineSegment(sketch, "E92.MirrorCS", {"start": v(0, -90) * mm, "end": v(0, -120) * mm, "construction": true});
            skPoint(sketch, "E93.MirrorP", {"position": v(0, -90) * mm});
            skArc(sketch, "E94.MirrorCS", {"start": v(-15, -120) * mm, "mid": v(0, -135) * mm, "end": v(15, -120) * mm});
            skLineSegment(sketch, "E95.MirrorCS", {"start": v(15, -108) * mm, "end": v(33, -90) * mm});
            skSolve(sketch);
        }
        {
            var Q0;
            Q0 = qSketchRegion(id + "F16", true);
            var Q1;
            Q1=makeQuery(id+"F2.opExtrude","CAP_FACE",FACE,{"disambiguationData":[OSD([sQuery(id+"F0.wireOp",EDGE,"E12"),sQuery(id+"F0.wireOp",EDGE,"E13"),sQuery(id+"F0.wireOp",EDGE,"E14"),sQuery(id+"F0.wireOp",EDGE,"E15"),sQuery(id+"F0.wireOp",EDGE,"E17.filletArc"),sQuery(id+"F0.wireOp",EDGE,"E18.filletArc"),sQuery(id+"F0.wireOp",EDGE,"E19.filletArc"),sQuery(id+"F0.wireOp",EDGE,"E20.filletArc"),sQuery(id+"F0.wireOp",EDGE,"E25.0"),sQuery(id+"F0.wireOp",EDGE,"E25.1"),sQuery(id+"F0.wireOp",EDGE,"E25.2"),sQuery(id+"F0.wireOp",EDGE,"E25.3"),sQuery(id+"F0.wireOp",EDGE,"E25.4"),sQuery(id+"F0.wireOp",EDGE,"E25.5"),sQuery(id+"F0.wireOp",EDGE,"E25.6"),sQuery(id+"F0.wireOp",EDGE,"E25.7")])],"isStart":false});
            extrude(context, id + "F17", {"entities" : qUnion([Q0]), "endBound" : BoundingType.UP_TO_SURFACE, "endBoundEntityFace" : qUnion([Q1]), "depth" : 25 * mm});
        }
    });
